# Revit family: Equal_Double_Bowl_Drop-in_ADA_Sink-Elkay-LRAD2918551_5_MR2
name_source: partatom
category: Plumbing Fixtures
units: mm (PartAtom-declared; Revit-internal decimal feet)

## family parameters
Cut with Voids When Loaded = No
Host = Face
Maintain Annotation Orientation = No
OmniClass Number = 23.45.05.14.14
OmniClass Title = Sinks/Lavatories
Part Type = Normal
Room Calculation Point = No
Round Connector Dimension = Use Diameter
Shared = No

## types (5) — shared parameters
Approx. Shipping Weight (lbs) = 16
Assembly Code = D2010410
Back Flange = 4.25 "
Bowl 1 Dimensions = 12 inch x 12 inch x 5 3/8 inch
Bowl 2 Dimensions = 12 inch x 12 inch x 5 3/8 inch
Bowl Depth = 5.375 "
Bowl Length 2 = 12 "
Bowl Length1 = 12 "
Bowl Width = 12 "
CL of Faucet Hole = 2.25 "
Cutting Length = 28.37 "
Cutting Width = 17.37 "
Darin and Pitch height = 0.65 "
Default Elevation = 48 "
Description = Elkay Lustertone Stainless Steel 29 inch x 18 inch x 5 1/2 inch Equal Double Bowl Top Mount ADA Sink
Distance B/W 2 Bowls = 1.25 "
Drain Location = Center
Drain Location Along X- Axis = 6 "
Drain Location Along Y- Axis = 6 "
Drain Size = 3.5 "
Front Flange = 1.75 "
Gauge = 18
Hole-2 = Yes
Hole-5 = No
Installation Type = Drop-in
Left Flange = 1.875 "
Length of Sink = 29 "
Main Material = Finish-Elkay-Stainless Steel
Manufacturer = Elkay Manufacturer Company
Manufacturer Brand = Elkay (by Zurn Elkay Water Solutions)
Masking Region for Bowl = 1.75 "
Number of Bowls = 2
Outlet Connection Size (inch) = 1.5 "
Product Documentation Link = https://www.elkayfiles.com
Product Installation Sheet URL = https://www.elkayfiles.com
Product Page URL = https://www.elkay.com
Product Weight (lbs) = 14
Product data URL = https://www.bimobject.com
R1 for Rim = 0.09 "
R2 for Rim = 0.06 "
Radius for Bowl = 1.76 "
Radius for cutting endge = 1.5 "
Repair Parts URL = https://www.elkayfiles.com
Right Flange = 1.875 "
Rim Height = 0.125 "
Sink Depth = 5.5 "
Sink Dimensions = 29 inch x 18 inch x  5 1/2 inch
U-channel Length along -X axis = 24 "
U-channel Length along -Y axis = 13 "
URL = https://www.elkay.com
Vertical Radius = 1.75 "
Waste Connection = No
Width of Sink = 18 "
zero-valued in all types: OS4

## per-type parameters (varying)
| type | Hole 2 | Hole-1 | Hole-3 | Hole-4 | ML2 | MR2 | Model | No of Hole configurations |
| LRAD2918651 (Single Bowl Drop-in ADA Sink) | 14.5 " | No | No | No | 0 | 0 | LRAD2918551 | 1 |
| LRAD2918652 (Single Bowl Drop-in ADA Sink) | 12.5 " | No | Yes | No | 0 | 1 | LRAD2918552 | 2 |
| LRAD2918653 (Single Bowl Drop-in ADA Sink) | 14.5 " | Yes | Yes | No | 1 | 1 | LRAD2918553 | 3 |
| LRAD2918654 (Single Bowl Drop-in ADA Sink) | 14.5 " | Yes | Yes | Yes | 1 | 1 | LRAD2918554 | 4 |
| LRAD291865MR2 (Single Bowl Drop-in ADA Sink) | 14.5 " | No | Yes | No | 0 | 1 | LRAD291855MR2 | 1 |

## geometry (parser evidence)
native form markers: Sweep x5
no freeform markers — native parametric forms only
